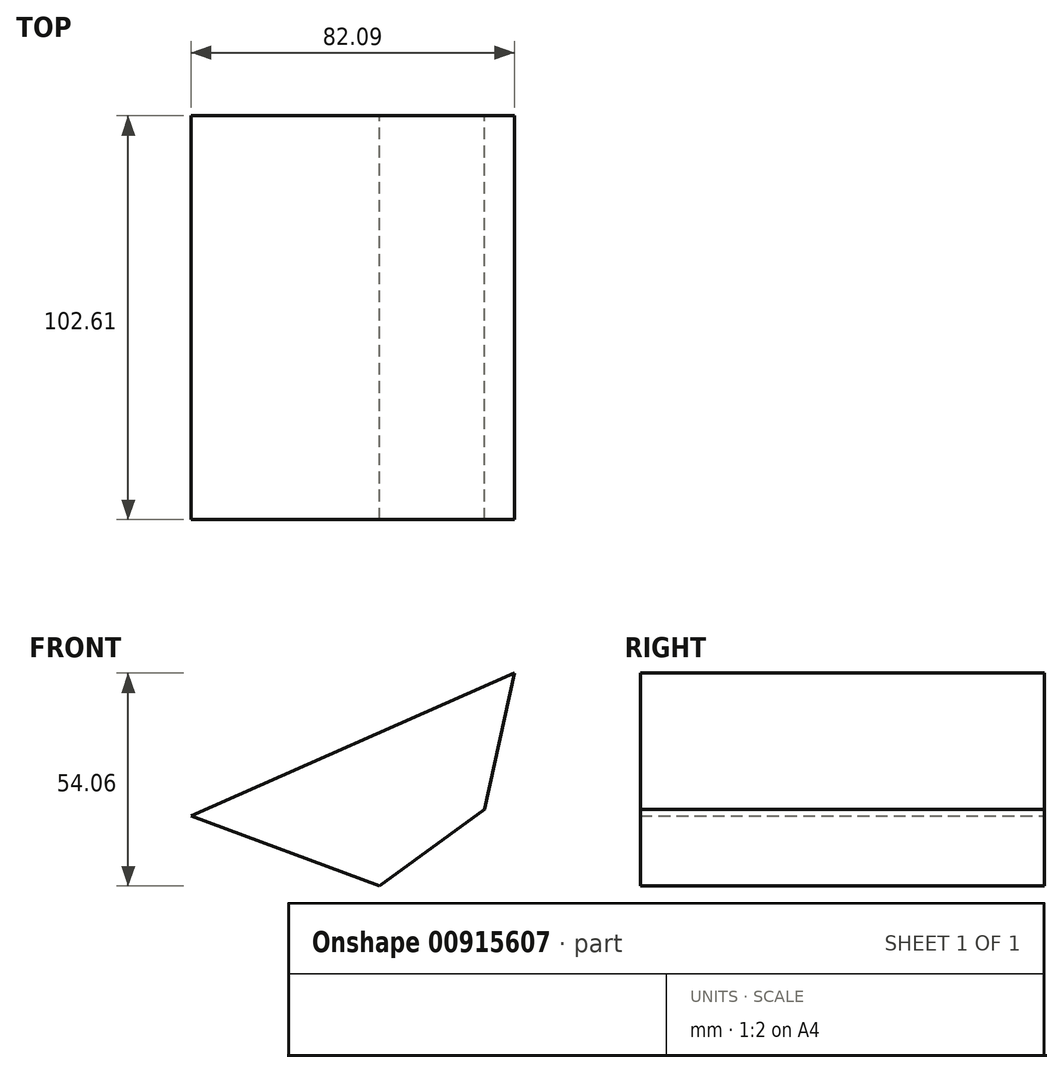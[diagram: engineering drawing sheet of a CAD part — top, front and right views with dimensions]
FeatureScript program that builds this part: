
annotation { "Feature Type Name" : "Feature", "Feature Type Description" : "" }
export const myFeature = defineFeature(function(context is Context, id is Id, definition is map)
    precondition{}
    {
        {
            var Q0;
            Q0=qCreatedBy(makeId("Front.planeOp"),FACE);
            var sketch = newSketch(context, id + "F0", { "sketchPlane" : qUnion([Q0])});
            skLineSegment(sketch, "E0", {"start": v(74.3, -28.95) * mm, "end": v(-7.8, -65.29) * mm});
            skLineSegment(sketch, "E1", {"start": v(-7.8, -65.29) * mm, "end": v(40, -83) * mm});
            skLineSegment(sketch, "E2", {"start": v(40, -83) * mm, "end": v(66.68, -63.53) * mm});
            skLineSegment(sketch, "E3", {"start": v(66.68, -63.53) * mm, "end": v(74.3, -28.95) * mm});
            skSolve(sketch);
        }
        {
            var Q0;
            Q0=makeQuery(id+"F0.imprint","IMPRINT",FACE,{"disambiguationData":[TD([[makeQuery(id+"F0.imprint","IMPRINT",EDGE,{"derivedFrom":sQuery(id+"F0.wireOp",EDGE,"E0")}),1.0]])]});
            extrude(context, id + "F1", {"entities" : qUnion([Q0]), "depth" : 102.6 * mm, "offsetDistance" : 25.4 * mm});
        }
    });
